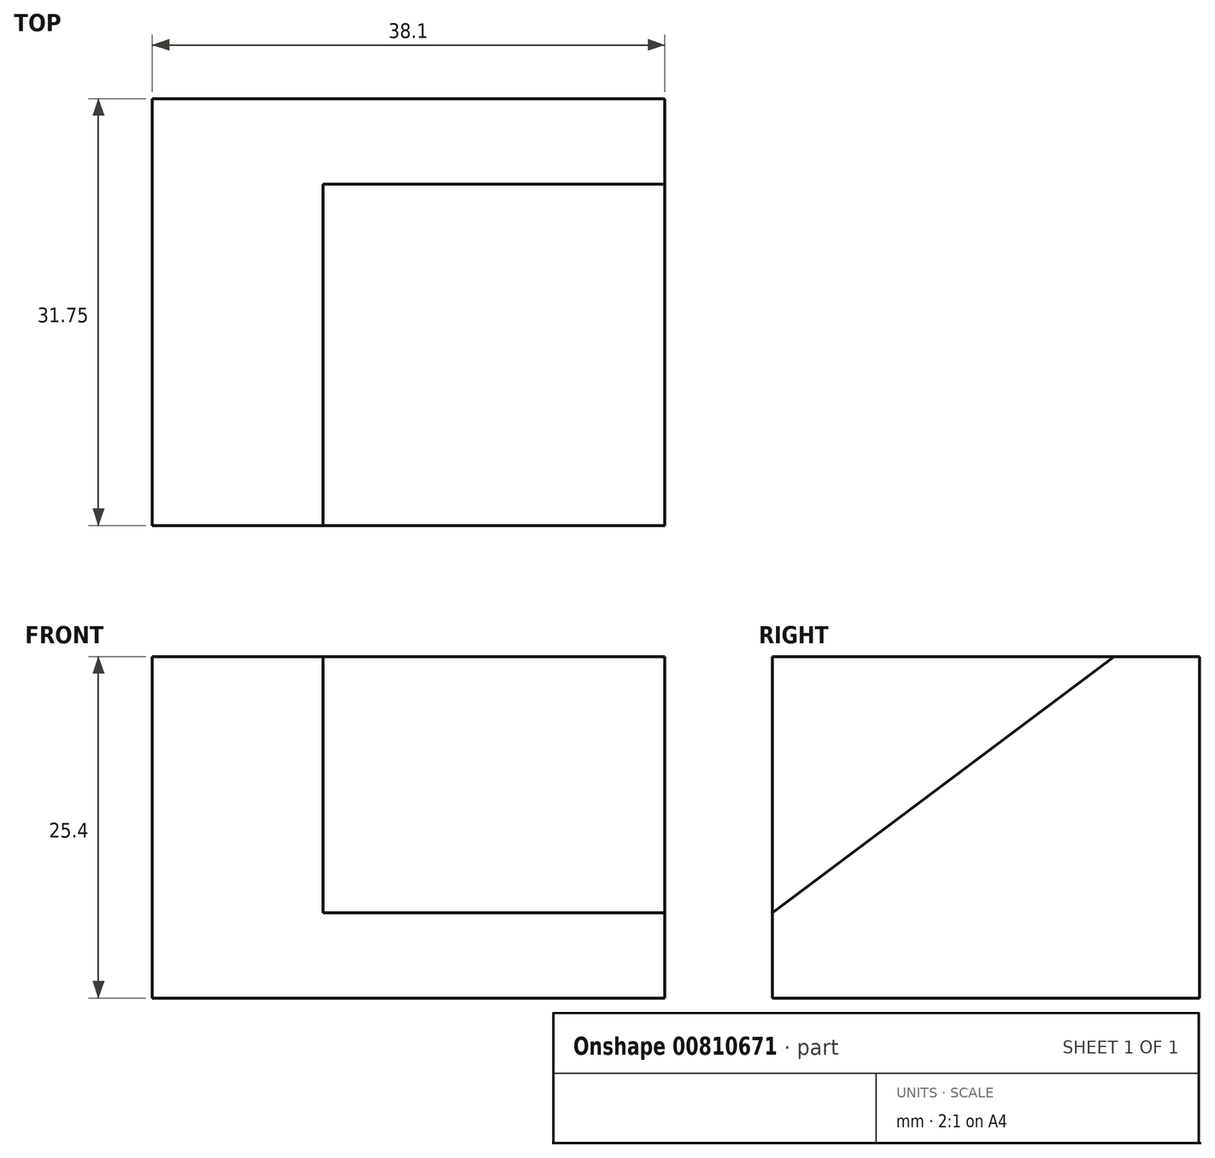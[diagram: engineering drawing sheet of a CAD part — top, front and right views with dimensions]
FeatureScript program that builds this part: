
annotation { "Feature Type Name" : "Feature", "Feature Type Description" : "" }
export const myFeature = defineFeature(function(context is Context, id is Id, definition is map)
    precondition{}
    {
        {
            var Q0;
            Q0=qCreatedBy(makeId("Top.planeOp"),FACE);
            var sketch = newSketch(context, id + "F0", { "sketchPlane" : qUnion([Q0])});
            skLineSegment(sketch, "E0.bottom", {"start": v(0, 0) * mm, "end": v(38.1, 0) * mm});
            skLineSegment(sketch, "E0.top", {"start": v(0, 31.75) * mm, "end": v(38.1, 31.75) * mm});
            skLineSegment(sketch, "E0.left", {"start": v(0, 0) * mm, "end": v(0, 31.75) * mm});
            skLineSegment(sketch, "E0.right", {"start": v(38.1, 0) * mm, "end": v(38.1, 31.75) * mm});
            skSolve(sketch);
        }
        {
            var Q0;
            Q0=makeQuery(id+"F0.imprint","IMPRINT",FACE,{"disambiguationData":[TD([[makeQuery(id+"F0.imprint","IMPRINT",EDGE,{"derivedFrom":sQuery(id+"F0.wireOp",EDGE,"E0.bottom")}),1.0]])]});
            extrude(context, id + "F1", {"entities" : qUnion([Q0]), "depth" : 25.4 * mm, "offsetDistance" : 25.4 * mm});
        }
        {
            var Q0;
            Q0=makeQuery(id+"F1.opExtrude","SWEPT_FACE",FACE,{"disambiguationData":[OSD([sQuery(id+"F0.wireOp",EDGE,"E0.right")])]});
            var sketch = newSketch(context, id + "F2", { "sketchPlane" : qUnion([Q0])});
            skLineSegment(sketch, "E1", {"start": v(0, 0) * mm, "end": v(0, 6.35) * mm});
            skLineSegment(sketch, "E2", {"start": v(31.75, 25.4) * mm, "end": v(25.4, 25.4) * mm});
            skLineSegment(sketch, "E3", {"start": v(0, 6.35) * mm, "end": v(25.4, 25.4) * mm});
            skSolve(sketch);
        }
        {
            var Q0;
            Q0 = qSketchRegion(id + "F2", true);
            var Q1;
            {var subQ0=sQuery(id+"F2.wireOp",EDGE,"E3");Q1=makeQuery(id+"F2.imprint","IMPRINT",FACE,{"disambiguationData":[TD([[makeQuery(id+"F2.imprint","IMPRINT",EDGE,{"derivedFrom":subQ0}),1.0]])]});}
            extrude(context, id + "F3", {"entities" : qUnion([Q0, Q1]), "operationType" : NewBodyOperationType.REMOVE, "oppositeDirection" : true, "depth" : 25.4 * mm, "offsetDistance" : 25.4 * mm});
        }
    });
